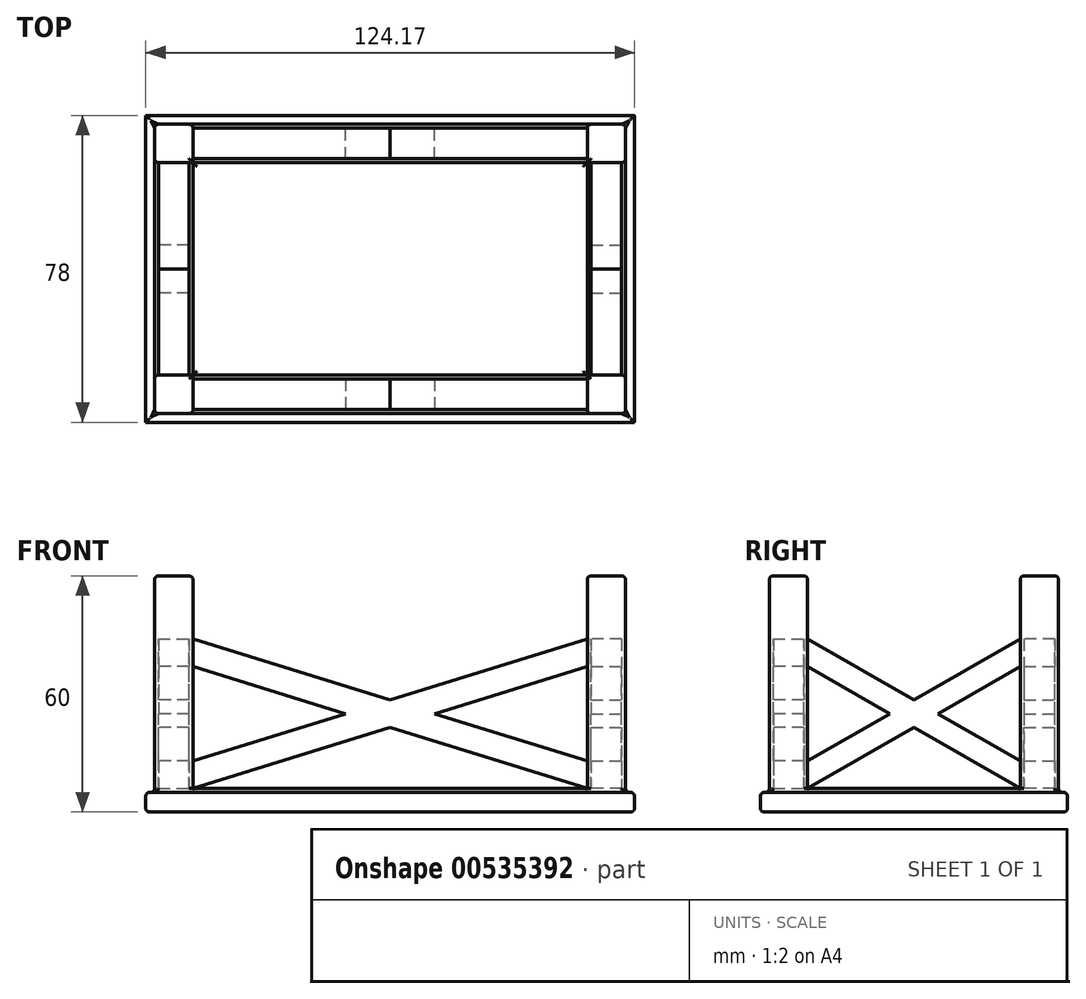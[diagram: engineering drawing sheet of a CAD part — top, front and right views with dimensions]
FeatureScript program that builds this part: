
annotation { "Feature Type Name" : "Feature", "Feature Type Description" : "" }
export const myFeature = defineFeature(function(context is Context, id is Id, definition is map)
    precondition{}
    {
        {
            var Q0;
            Q0=qCreatedBy(makeId("Top.planeOp"),FACE);
            var sketch = newSketch(context, id + "F0", { "sketchPlane" : qUnion([Q0])});
            skLineSegment(sketch, "E0.bottom", {"start": v(-35.73, 48.82) * mm, "end": v(88.44, 48.82) * mm});
            skLineSegment(sketch, "E0.top", {"start": v(-35.73, -29.18) * mm, "end": v(88.44, -29.18) * mm});
            skLineSegment(sketch, "E0.left", {"start": v(-35.73, 48.82) * mm, "end": v(-35.73, -29.18) * mm});
            skLineSegment(sketch, "E0.right", {"start": v(88.44, 48.82) * mm, "end": v(88.44, -29.18) * mm});
            skPoint(sketch, "E1", {"position": v(26.36, -29.18) * mm});
            skSolve(sketch);
        }
        {
            var Q0;
            Q0=qSketchRegion(id+"F0",true);
            extrude(context, id + "F1", {"entities" : qUnion([Q0]), "depth" : 5 * mm});
        }
        {
            var Q0;
            Q0=makeQuery(id+"F1.opExtrude","CAP_FACE",FACE,{"disambiguationData":[OSD([sQuery(id+"F0.wireOp",EDGE,"E0.bottom"),sQuery(id+"F0.wireOp",EDGE,"E0.top"),sQuery(id+"F0.wireOp",EDGE,"E0.left"),sQuery(id+"F0.wireOp",EDGE,"E0.right")])],"isStart":false});
            var sketch = newSketch(context, id + "F2", { "sketchPlane" : qUnion([Q0])});
            skLineSegment(sketch, "E2.bottom", {"start": v(-35.73, -29.18) * mm, "end": v(-23.73, -29.18) * mm, "construction": true});
            skLineSegment(sketch, "E2.top", {"start": v(-35.73, -17.18) * mm, "end": v(-23.73, -17.18) * mm, "construction": true});
            skLineSegment(sketch, "E2.left", {"start": v(-35.73, -29.18) * mm, "end": v(-35.73, -17.18) * mm, "construction": true});
            skLineSegment(sketch, "E2.right", {"start": v(-23.73, -29.18) * mm, "end": v(-23.73, -17.18) * mm, "construction": true});
            skLineSegment(sketch, "E3.bottom", {"start": v(88.44, 48.82) * mm, "end": v(76.44, 48.82) * mm, "construction": true});
            skLineSegment(sketch, "E3.top", {"start": v(88.44, 36.82) * mm, "end": v(76.44, 36.82) * mm, "construction": true});
            skLineSegment(sketch, "E3.left", {"start": v(88.44, 48.82) * mm, "end": v(88.44, 36.82) * mm, "construction": true});
            skLineSegment(sketch, "E3.right", {"start": v(76.44, 48.82) * mm, "end": v(76.44, 36.82) * mm, "construction": true});
            skLineSegment(sketch, "E4.bottom", {"start": v(88.44, -29.18) * mm, "end": v(76.44, -29.18) * mm, "construction": true});
            skLineSegment(sketch, "E4.top", {"start": v(88.44, -17.18) * mm, "end": v(76.44, -17.18) * mm, "construction": true});
            skLineSegment(sketch, "E4.left", {"start": v(88.44, -29.18) * mm, "end": v(88.44, -17.18) * mm, "construction": true});
            skLineSegment(sketch, "E4.right", {"start": v(76.44, -29.18) * mm, "end": v(76.44, -17.18) * mm, "construction": true});
            skLineSegment(sketch, "E5.bottom", {"start": v(-35.73, 48.82) * mm, "end": v(-23.73, 48.82) * mm, "construction": true});
            skLineSegment(sketch, "E5.top", {"start": v(-35.73, 36.82) * mm, "end": v(-23.73, 36.82) * mm, "construction": true});
            skLineSegment(sketch, "E5.left", {"start": v(-35.73, 48.82) * mm, "end": v(-35.73, 36.82) * mm, "construction": true});
            skLineSegment(sketch, "E5.right", {"start": v(-23.73, 48.82) * mm, "end": v(-23.73, 36.82) * mm, "construction": true});
            skLineSegment(sketch, "E6.bottom", {"start": v(-23.73, 36.82) * mm, "end": v(-33.48, 36.82) * mm});
            skLineSegment(sketch, "E6.top", {"start": v(-23.73, 46.57) * mm, "end": v(-33.48, 46.57) * mm});
            skLineSegment(sketch, "E6.left", {"start": v(-23.73, 36.82) * mm, "end": v(-23.73, 46.57) * mm});
            skLineSegment(sketch, "E6.right", {"start": v(-33.48, 36.82) * mm, "end": v(-33.48, 46.57) * mm});
            skLineSegment(sketch, "E7.bottom", {"start": v(-23.73, -17.18) * mm, "end": v(-33.48, -17.18) * mm});
            skLineSegment(sketch, "E7.top", {"start": v(-23.73, -26.93) * mm, "end": v(-33.48, -26.93) * mm});
            skLineSegment(sketch, "E7.left", {"start": v(-23.73, -17.18) * mm, "end": v(-23.73, -26.93) * mm});
            skLineSegment(sketch, "E7.right", {"start": v(-33.48, -17.18) * mm, "end": v(-33.48, -26.93) * mm});
            skLineSegment(sketch, "E8.bottom", {"start": v(76.44, 36.82) * mm, "end": v(86.2, 36.82) * mm});
            skLineSegment(sketch, "E8.top", {"start": v(76.44, 46.57) * mm, "end": v(86.2, 46.57) * mm});
            skLineSegment(sketch, "E8.left", {"start": v(76.44, 36.82) * mm, "end": v(76.44, 46.57) * mm});
            skLineSegment(sketch, "E8.right", {"start": v(86.2, 36.82) * mm, "end": v(86.2, 46.57) * mm});
            skLineSegment(sketch, "E9.bottom", {"start": v(76.44, -17.18) * mm, "end": v(86.2, -17.18) * mm});
            skLineSegment(sketch, "E9.top", {"start": v(76.44, -26.93) * mm, "end": v(86.2, -26.93) * mm});
            skLineSegment(sketch, "E9.left", {"start": v(76.44, -17.18) * mm, "end": v(76.44, -26.93) * mm});
            skLineSegment(sketch, "E9.right", {"start": v(86.2, -17.18) * mm, "end": v(86.2, -26.93) * mm});
            skSolve(sketch);
        }
        {
            var Q0;
            Q0=qSketchRegion(id+"F2",true);
            extrude(context, id + "F3", {"entities" : qUnion([Q0]), "operationType" : NewBodyOperationType.ADD, "depth" : 55 * mm});
        }
        {
            var Q0;
            Q0=makeQuery(id+"F3.opExtrude","SWEPT_FACE",FACE,{"disambiguationData":[OSD([sQuery(id+"F2.wireOp",EDGE,"E7.left")])]});
            var sketch = newSketch(context, id + "F4", { "sketchPlane" : qUnion([Q0])});
            skLineSegment(sketch, "E10.bottom", {"start": v(-25.93, 59) * mm, "end": v(-18.18, 59) * mm, "construction": true});
            skLineSegment(sketch, "E10.top", {"start": v(-25.93, 44) * mm, "end": v(-18.18, 44) * mm, "construction": true});
            skLineSegment(sketch, "E10.left", {"start": v(-25.93, 59) * mm, "end": v(-25.93, 44) * mm, "construction": true});
            skLineSegment(sketch, "E10.right", {"start": v(-18.18, 59) * mm, "end": v(-18.18, 44) * mm, "construction": true});
            skLineSegment(sketch, "E11.bottom", {"start": v(-25.93, 44) * mm, "end": v(-18.18, 44) * mm});
            skLineSegment(sketch, "E11.top", {"start": v(-25.93, 6) * mm, "end": v(-18.18, 6) * mm});
            skLineSegment(sketch, "E11.left", {"start": v(-25.93, 44) * mm, "end": v(-25.93, 6) * mm});
            skLineSegment(sketch, "E11.right", {"start": v(-18.18, 44) * mm, "end": v(-18.18, 6) * mm});
            skSolve(sketch);
        }
        {
            var Q0;
            Q0=qSketchRegion(id+"F4",true);
            extrude(context, id + "F5", {"entities" : qUnion([Q0]), "operationType" : NewBodyOperationType.ADD, "endBound" : BoundingType.UP_TO_NEXT, "depth" : 100.17 * mm});
        }
        {
            var Q0;
            Q0=makeQuery(id+"F5.opExtrude","SWEPT_FACE",FACE,{"disambiguationData":[OSD([sQuery(id+"F4.wireOp",EDGE,"E11.left")])]});
            var sketch = newSketch(context, id + "F6", { "sketchPlane" : qUnion([Q0])});
            skPoint(sketch, "E12", {"position": v(-23.73, 44) * mm});
            skPoint(sketch, "E13", {"position": v(-23.73, 37) * mm});
            skPoint(sketch, "E14", {"position": v(-23.73, 6) * mm});
            skPoint(sketch, "E15", {"position": v(-23.73, 13) * mm});
            skPoint(sketch, "E16", {"position": v(76.44, 44) * mm});
            skPoint(sketch, "E17", {"position": v(76.44, 37) * mm});
            skPoint(sketch, "E18", {"position": v(76.44, 6) * mm});
            skPoint(sketch, "E19", {"position": v(76.44, 13) * mm});
            skPoint(sketch, "E20", {"position": v(26.36, 28.5) * mm});
            skPoint(sketch, "E21", {"position": v(26.36, 21.5) * mm});
            skPoint(sketch, "E22", {"position": v(15.05, 25) * mm});
            skPoint(sketch, "E23", {"position": v(37.67, 25) * mm});
            skLineSegment(sketch, "E24", {"start": v(-23.73, 44) * mm, "end": v(76.44, 44) * mm});
            skLineSegment(sketch, "E25", {"start": v(26.36, 28.5) * mm, "end": v(76.44, 44) * mm});
            skLineSegment(sketch, "E26", {"start": v(-23.73, 44) * mm, "end": v(26.36, 28.5) * mm});
            skLineSegment(sketch, "E27", {"start": v(76.44, 37) * mm, "end": v(76.44, 13) * mm});
            skLineSegment(sketch, "E28", {"start": v(76.44, 13.06) * mm, "end": v(37.67, 25) * mm});
            skLineSegment(sketch, "E29", {"start": v(15.05, 25) * mm, "end": v(-23.73, 37) * mm});
            skLineSegment(sketch, "E30", {"start": v(15.05, 25) * mm, "end": v(-23.73, 13) * mm});
            skLineSegment(sketch, "E31", {"start": v(-23.73, 13) * mm, "end": v(-23.73, 37) * mm});
            skLineSegment(sketch, "E32", {"start": v(-23.73, 6) * mm, "end": v(76.44, 6) * mm});
            skLineSegment(sketch, "E33", {"start": v(26.36, 21.5) * mm, "end": v(76.44, 6) * mm});
            skLineSegment(sketch, "E34", {"start": v(26.36, 21.5) * mm, "end": v(-23.73, 6) * mm});
            skLineSegment(sketch, "E35", {"start": v(37.67, 25) * mm, "end": v(76.44, 37) * mm});
            skLineSegment(sketch, "E36", {"start": v(76.44, 37) * mm, "end": v(76.44, 13.06) * mm});
            skSolve(sketch);
        }
        {
            var Q0;
            Q0=qSketchRegion(id+"F6",true);
            extrude(context, id + "F7", {"entities" : qUnion([Q0]), "operationType" : NewBodyOperationType.REMOVE, "endBound" : BoundingType.UP_TO_NEXT, "oppositeDirection" : true, "depth" : 25 * mm});
        }
        {
            var Q0;
            Q0=makeQuery(id+"F3.opExtrude","SWEPT_FACE",FACE,{"disambiguationData":[OSD([sQuery(id+"F2.wireOp",EDGE,"E8.left")])]});
            var sketch = newSketch(context, id + "F8", { "sketchPlane" : qUnion([Q0])});
            skLineSegment(sketch, "E37.bottom", {"start": v(-45.57, 59) * mm, "end": v(-37.82, 59) * mm, "construction": true});
            skLineSegment(sketch, "E37.top", {"start": v(-45.57, 44) * mm, "end": v(-37.82, 44) * mm, "construction": true});
            skLineSegment(sketch, "E37.left", {"start": v(-45.57, 59) * mm, "end": v(-45.57, 44) * mm, "construction": true});
            skLineSegment(sketch, "E37.right", {"start": v(-37.82, 59) * mm, "end": v(-37.82, 44) * mm, "construction": true});
            skLineSegment(sketch, "E38.bottom", {"start": v(-45.57, 44) * mm, "end": v(-37.82, 44) * mm});
            skLineSegment(sketch, "E38.top", {"start": v(-45.57, 6) * mm, "end": v(-37.82, 6) * mm});
            skLineSegment(sketch, "E38.left", {"start": v(-45.57, 44) * mm, "end": v(-45.57, 6) * mm});
            skLineSegment(sketch, "E38.right", {"start": v(-37.82, 44) * mm, "end": v(-37.82, 6) * mm});
            skSolve(sketch);
        }
        {
            var Q0;
            Q0=qSketchRegion(id+"F8",true);
            extrude(context, id + "F9", {"entities" : qUnion([Q0]), "operationType" : NewBodyOperationType.ADD, "endBound" : BoundingType.UP_TO_NEXT, "depth" : 25 * mm});
        }
        {
            var Q0;
            Q0=makeQuery(id+"F9.opExtrude","SWEPT_FACE",FACE,{"disambiguationData":[OSD([sQuery(id+"F8.wireOp",EDGE,"E38.left")])]});
            var sketch = newSketch(context, id + "F10", { "sketchPlane" : qUnion([Q0])});
            skPoint(sketch, "E39", {"position": v(-76.44, 44) * mm});
            skPoint(sketch, "E40", {"position": v(-76.44, 37) * mm});
            skPoint(sketch, "E41", {"position": v(-76.44, 13) * mm});
            skPoint(sketch, "E42", {"position": v(-76.44, 6) * mm});
            skPoint(sketch, "E43", {"position": v(23.73, 44) * mm});
            skPoint(sketch, "E44", {"position": v(23.73, 37) * mm});
            skPoint(sketch, "E45", {"position": v(23.73, 13) * mm});
            skPoint(sketch, "E46", {"position": v(23.73, 6) * mm});
            skLineSegment(sketch, "E47", {"start": v(-76.44, 37) * mm, "end": v(23.73, 6) * mm, "construction": true});
            skLineSegment(sketch, "E48", {"start": v(-76.44, 44) * mm, "end": v(23.73, 13) * mm, "construction": true});
            skLineSegment(sketch, "E49", {"start": v(23.73, 44) * mm, "end": v(-76.44, 13) * mm, "construction": true});
            skLineSegment(sketch, "E50", {"start": v(-76.44, 6) * mm, "end": v(23.73, 37) * mm, "construction": true});
            skLineSegment(sketch, "E51", {"start": v(-76.44, 44) * mm, "end": v(-26.36, 28.5) * mm});
            skLineSegment(sketch, "E52", {"start": v(-26.36, 28.5) * mm, "end": v(23.73, 44) * mm});
            skLineSegment(sketch, "E53", {"start": v(-76.44, 44) * mm, "end": v(23.73, 44) * mm});
            skLineSegment(sketch, "E54", {"start": v(-76.44, 13) * mm, "end": v(-76.44, 37) * mm});
            skLineSegment(sketch, "E55", {"start": v(-76.44, 37) * mm, "end": v(-37.67, 25) * mm});
            skLineSegment(sketch, "E56", {"start": v(-37.67, 25) * mm, "end": v(-76.44, 13) * mm});
            skLineSegment(sketch, "E57", {"start": v(-76.44, 6) * mm, "end": v(23.73, 6) * mm});
            skLineSegment(sketch, "E58", {"start": v(-26.36, 21.5) * mm, "end": v(23.73, 6) * mm});
            skLineSegment(sketch, "E59", {"start": v(-76.44, 6) * mm, "end": v(-26.36, 21.5) * mm});
            skLineSegment(sketch, "E60", {"start": v(23.73, 37) * mm, "end": v(23.73, 13) * mm});
            skLineSegment(sketch, "E61", {"start": v(23.73, 13) * mm, "end": v(-15.05, 25) * mm});
            skLineSegment(sketch, "E62", {"start": v(-15.05, 25) * mm, "end": v(23.73, 37) * mm});
            skSolve(sketch);
        }
        {
            var Q0;
            Q0=qSketchRegion(id+"F10",true);
            extrude(context, id + "F11", {"entities" : qUnion([Q0]), "operationType" : NewBodyOperationType.REMOVE, "endBound" : BoundingType.UP_TO_NEXT, "oppositeDirection" : true, "depth" : 25 * mm});
        }
        {
            var Q0;
            Q0=makeQuery(id+"F3.opExtrude","SWEPT_FACE",FACE,{"disambiguationData":[OSD([sQuery(id+"F2.wireOp",EDGE,"E6.bottom")])]});
            var sketch = newSketch(context, id + "F12", { "sketchPlane" : qUnion([Q0])});
            skLineSegment(sketch, "E63.bottom", {"start": v(-32.48, 59) * mm, "end": v(-24.73, 59) * mm, "construction": true});
            skLineSegment(sketch, "E63.top", {"start": v(-32.48, 44) * mm, "end": v(-24.73, 44) * mm, "construction": true});
            skLineSegment(sketch, "E63.left", {"start": v(-32.48, 59) * mm, "end": v(-32.48, 44) * mm, "construction": true});
            skLineSegment(sketch, "E63.right", {"start": v(-24.73, 59) * mm, "end": v(-24.73, 44) * mm, "construction": true});
            skLineSegment(sketch, "E64.bottom", {"start": v(-32.48, 44) * mm, "end": v(-24.73, 44) * mm});
            skLineSegment(sketch, "E64.top", {"start": v(-32.48, 6) * mm, "end": v(-24.73, 6) * mm});
            skLineSegment(sketch, "E64.left", {"start": v(-32.48, 44) * mm, "end": v(-32.48, 6) * mm});
            skLineSegment(sketch, "E64.right", {"start": v(-24.73, 44) * mm, "end": v(-24.73, 6) * mm});
            skSolve(sketch);
        }
        {
            var Q0;
            Q0=qSketchRegion(id+"F12",true);
            extrude(context, id + "F13", {"entities" : qUnion([Q0]), "operationType" : NewBodyOperationType.ADD, "endBound" : BoundingType.UP_TO_NEXT, "depth" : 25 * mm});
        }
        {
            var Q0;
            Q0=makeQuery(id+"F13.opExtrude","SWEPT_FACE",FACE,{"disambiguationData":[OSD([sQuery(id+"F12.wireOp",EDGE,"E64.left")])]});
            var sketch = newSketch(context, id + "F14", { "sketchPlane" : qUnion([Q0])});
            skPoint(sketch, "E65", {"position": v(-36.82, 44) * mm});
            skPoint(sketch, "E66", {"position": v(-36.82, 37) * mm});
            skPoint(sketch, "E67", {"position": v(-36.82, 13) * mm});
            skPoint(sketch, "E68", {"position": v(-36.82, 6) * mm});
            skPoint(sketch, "E69", {"position": v(17.18, 6) * mm});
            skPoint(sketch, "E70", {"position": v(17.18, 13) * mm});
            skPoint(sketch, "E71", {"position": v(17.18, 37) * mm});
            skPoint(sketch, "E72", {"position": v(17.18, 44) * mm});
            skLineSegment(sketch, "E73", {"start": v(-36.82, 37) * mm, "end": v(17.18, 6) * mm, "construction": true});
            skLineSegment(sketch, "E74", {"start": v(17.18, 13) * mm, "end": v(-36.82, 44) * mm, "construction": true});
            skLineSegment(sketch, "E75", {"start": v(-36.82, 13) * mm, "end": v(17.18, 44) * mm, "construction": true});
            skLineSegment(sketch, "E76", {"start": v(17.18, 37) * mm, "end": v(-36.82, 6) * mm, "construction": true});
            skLineSegment(sketch, "E77", {"start": v(-36.82, 44) * mm, "end": v(17.18, 44) * mm});
            skLineSegment(sketch, "E78", {"start": v(-9.82, 28.5) * mm, "end": v(17.18, 44) * mm});
            skLineSegment(sketch, "E79", {"start": v(-9.82, 28.5) * mm, "end": v(-36.82, 44) * mm});
            skLineSegment(sketch, "E80", {"start": v(-36.82, 37) * mm, "end": v(-36.82, 13) * mm});
            skLineSegment(sketch, "E81", {"start": v(-36.82, 13) * mm, "end": v(-15.92, 25) * mm});
            skLineSegment(sketch, "E82", {"start": v(-15.92, 25) * mm, "end": v(-36.82, 37) * mm});
            skLineSegment(sketch, "E83", {"start": v(17.18, 37) * mm, "end": v(17.18, 13) * mm});
            skLineSegment(sketch, "E84", {"start": v(17.18, 13) * mm, "end": v(-3.72, 25) * mm});
            skLineSegment(sketch, "E85", {"start": v(17.18, 37) * mm, "end": v(-3.72, 25) * mm});
            skLineSegment(sketch, "E86", {"start": v(-36.82, 6) * mm, "end": v(17.18, 6) * mm});
            skLineSegment(sketch, "E87", {"start": v(17.18, 6) * mm, "end": v(-9.82, 21.5) * mm});
            skLineSegment(sketch, "E88", {"start": v(-36.82, 6) * mm, "end": v(-9.82, 21.5) * mm});
            skSolve(sketch);
        }
        {
            var Q0;
            Q0=qSketchRegion(id+"F14",true);
            extrude(context, id + "F15", {"entities" : qUnion([Q0]), "operationType" : NewBodyOperationType.REMOVE, "endBound" : BoundingType.UP_TO_NEXT, "oppositeDirection" : true, "depth" : 25 * mm});
        }
        {
            var Q0;
            Q0=makeQuery(id+"F3.opExtrude","SWEPT_FACE",FACE,{"disambiguationData":[OSD([sQuery(id+"F2.wireOp",EDGE,"E9.bottom")])]});
            var sketch = newSketch(context, id + "F16", { "sketchPlane" : qUnion([Q0])});
            skLineSegment(sketch, "E89.bottom", {"start": v(-85.2, 59) * mm, "end": v(-77.44, 59) * mm, "construction": true});
            skLineSegment(sketch, "E89.top", {"start": v(-85.2, 44) * mm, "end": v(-77.44, 44) * mm, "construction": true});
            skLineSegment(sketch, "E89.left", {"start": v(-85.2, 59) * mm, "end": v(-85.2, 44) * mm, "construction": true});
            skLineSegment(sketch, "E89.right", {"start": v(-77.44, 59) * mm, "end": v(-77.44, 44) * mm, "construction": true});
            skLineSegment(sketch, "E90.bottom", {"start": v(-85.2, 44) * mm, "end": v(-77.44, 44) * mm});
            skLineSegment(sketch, "E90.top", {"start": v(-85.2, 6) * mm, "end": v(-77.44, 6) * mm});
            skLineSegment(sketch, "E90.left", {"start": v(-85.2, 44) * mm, "end": v(-85.2, 6) * mm});
            skLineSegment(sketch, "E90.right", {"start": v(-77.44, 44) * mm, "end": v(-77.44, 6) * mm});
            skSolve(sketch);
        }
        {
            var Q0;
            Q0=qSketchRegion(id+"F16",true);
            extrude(context, id + "F17", {"entities" : qUnion([Q0]), "operationType" : NewBodyOperationType.ADD, "endBound" : BoundingType.UP_TO_NEXT, "depth" : 25 * mm});
        }
        {
            var Q0;
            Q0=makeQuery(id+"F17.opExtrude","SWEPT_FACE",FACE,{"disambiguationData":[OSD([sQuery(id+"F16.wireOp",EDGE,"E90.left")])]});
            var sketch = newSketch(context, id + "F18", { "sketchPlane" : qUnion([Q0])});
            skPoint(sketch, "E91", {"position": v(-17.18, 44) * mm});
            skPoint(sketch, "E92", {"position": v(-17.18, 37) * mm});
            skPoint(sketch, "E93", {"position": v(-17.18, 13) * mm});
            skPoint(sketch, "E94", {"position": v(-17.18, 6) * mm});
            skPoint(sketch, "E95", {"position": v(36.82, 44) * mm});
            skPoint(sketch, "E96", {"position": v(36.82, 37) * mm});
            skPoint(sketch, "E97", {"position": v(36.82, 13) * mm});
            skPoint(sketch, "E98", {"position": v(36.82, 6) * mm});
            skLineSegment(sketch, "E99", {"start": v(-17.18, 44) * mm, "end": v(36.82, 13) * mm, "construction": true});
            skLineSegment(sketch, "E100", {"start": v(36.82, 6) * mm, "end": v(-17.18, 37) * mm, "construction": true});
            skLineSegment(sketch, "E101", {"start": v(36.82, 44) * mm, "end": v(-17.18, 13) * mm, "construction": true});
            skLineSegment(sketch, "E102", {"start": v(-17.18, 6) * mm, "end": v(36.82, 37) * mm, "construction": true});
            skLineSegment(sketch, "E103", {"start": v(-17.18, 44) * mm, "end": v(36.82, 44) * mm});
            skLineSegment(sketch, "E104", {"start": v(36.82, 44) * mm, "end": v(9.82, 28.5) * mm});
            skLineSegment(sketch, "E105", {"start": v(9.82, 28.5) * mm, "end": v(-17.18, 44) * mm});
            skLineSegment(sketch, "E106", {"start": v(-17.18, 37) * mm, "end": v(-17.18, 13) * mm});
            skLineSegment(sketch, "E107", {"start": v(-17.18, 13) * mm, "end": v(3.72, 25) * mm});
            skLineSegment(sketch, "E108", {"start": v(-17.18, 37) * mm, "end": v(3.72, 25) * mm});
            skLineSegment(sketch, "E109", {"start": v(36.82, 37) * mm, "end": v(36.82, 13) * mm});
            skLineSegment(sketch, "E110", {"start": v(36.82, 13) * mm, "end": v(15.92, 25) * mm});
            skLineSegment(sketch, "E111", {"start": v(15.92, 25) * mm, "end": v(36.82, 37) * mm});
            skLineSegment(sketch, "E112", {"start": v(-17.18, 6) * mm, "end": v(36.82, 6) * mm});
            skLineSegment(sketch, "E113", {"start": v(36.82, 6) * mm, "end": v(9.82, 21.5) * mm});
            skLineSegment(sketch, "E114", {"start": v(9.82, 21.5) * mm, "end": v(-17.18, 6) * mm});
            skSolve(sketch);
        }
        {
            var Q0;
            Q0=qSketchRegion(id+"F18",true);
            extrude(context, id + "F19", {"entities" : qUnion([Q0]), "operationType" : NewBodyOperationType.REMOVE, "endBound" : BoundingType.UP_TO_NEXT, "oppositeDirection" : true, "depth" : 25 * mm});
        }
        {
            var Q0;
            Q0=makeQuery(id+"F15.boolean.opBoolean","MERGE",FACE,{"derivedFrom":[makeQuery(id+"F3.opExtrude","SWEPT_FACE",FACE,{"disambiguationData":[OSD([sQuery(id+"F2.wireOp",EDGE,"E7.bottom")])]}),makeQuery(id+"F15.opExtrude","SWEPT_FACE",FACE,{"disambiguationData":[OSD([sQuery(id+"F14.wireOp",EDGE,"E83")])]})]});
            var sketch = newSketch(context, id + "F20", { "sketchPlane" : qUnion([Q0])});
            skLineSegment(sketch, "E115.bottom", {"start": v(33.48, 5) * mm, "end": v(23.73, 5) * mm});
            skLineSegment(sketch, "E115.top", {"start": v(33.48, 6) * mm, "end": v(23.73, 6) * mm});
            skLineSegment(sketch, "E115.left", {"start": v(33.48, 5) * mm, "end": v(33.48, 6) * mm});
            skLineSegment(sketch, "E115.right", {"start": v(23.73, 5) * mm, "end": v(23.73, 6) * mm});
            skSolve(sketch);
        }
        {
            var Q0;
            Q0=qSketchRegion(id+"F20",true);
            extrude(context, id + "F21", {"entities" : qUnion([Q0]), "operationType" : NewBodyOperationType.ADD, "endBound" : BoundingType.UP_TO_NEXT, "depth" : 25 * mm});
        }
        {
            var Q0;
            Q0=makeQuery(id+"F21.boolean.opBoolean","MERGE",FACE,{"derivedFrom":[makeQuery(id+"F7.boolean.opBoolean","MERGE",FACE,{"derivedFrom":[makeQuery(id+"F3.opExtrude","SWEPT_FACE",FACE,{"disambiguationData":[OSD([sQuery(id+"F2.wireOp",EDGE,"E7.left")])]}),makeQuery(id+"F7.opExtrude","SWEPT_FACE",FACE,{"disambiguationData":[OSD([sQuery(id+"F6.wireOp",EDGE,"E31")])]})]}),makeQuery(id+"F11.boolean.opBoolean","MERGE",FACE,{"derivedFrom":[makeQuery(id+"F3.opExtrude","SWEPT_FACE",FACE,{"disambiguationData":[OSD([sQuery(id+"F2.wireOp",EDGE,"E6.left")])]}),makeQuery(id+"F11.opExtrude","SWEPT_FACE",FACE,{"disambiguationData":[OSD([sQuery(id+"F10.wireOp",EDGE,"E60")])]})]}),makeQuery(id+"F21.opExtrude","SWEPT_FACE",FACE,{"disambiguationData":[OSD([sQuery(id+"F20.wireOp",EDGE,"E115.right")])]})]});
            var sketch = newSketch(context, id + "F22", { "sketchPlane" : qUnion([Q0])});
            skLineSegment(sketch, "E116.bottom", {"start": v(46.57, 5) * mm, "end": v(36.82, 5) * mm});
            skLineSegment(sketch, "E116.top", {"start": v(46.57, 6) * mm, "end": v(36.82, 6) * mm});
            skLineSegment(sketch, "E116.left", {"start": v(46.57, 5) * mm, "end": v(46.57, 6) * mm});
            skLineSegment(sketch, "E116.right", {"start": v(36.82, 5) * mm, "end": v(36.82, 6) * mm});
            skSolve(sketch);
        }
        {
            var Q0;
            Q0=qSketchRegion(id+"F22",true);
            extrude(context, id + "F23", {"entities" : qUnion([Q0]), "operationType" : NewBodyOperationType.ADD, "endBound" : BoundingType.UP_TO_NEXT, "depth" : 25 * mm});
        }
        {
            var Q0;
            Q0=makeQuery(id+"F23.boolean.opBoolean","MERGE",FACE,{"derivedFrom":[makeQuery(id+"F19.boolean.opBoolean","MERGE",FACE,{"derivedFrom":[makeQuery(id+"F3.opExtrude","SWEPT_FACE",FACE,{"disambiguationData":[OSD([sQuery(id+"F2.wireOp",EDGE,"E8.bottom")])]}),makeQuery(id+"F19.opExtrude","SWEPT_FACE",FACE,{"disambiguationData":[OSD([sQuery(id+"F18.wireOp",EDGE,"E109")])]})]}),makeQuery(id+"F23.opExtrude","SWEPT_FACE",FACE,{"disambiguationData":[OSD([sQuery(id+"F22.wireOp",EDGE,"E116.right")])]})]});
            var sketch = newSketch(context, id + "F24", { "sketchPlane" : qUnion([Q0])});
            skLineSegment(sketch, "E117.bottom", {"start": v(86.2, 5) * mm, "end": v(76.44, 5) * mm});
            skLineSegment(sketch, "E117.top", {"start": v(86.2, 6) * mm, "end": v(76.44, 6) * mm});
            skLineSegment(sketch, "E117.left", {"start": v(86.2, 5) * mm, "end": v(86.2, 6) * mm});
            skLineSegment(sketch, "E117.right", {"start": v(76.44, 5) * mm, "end": v(76.44, 6) * mm});
            skSolve(sketch);
        }
        {
            var Q0;
            Q0=qSketchRegion(id+"F24",true);
            extrude(context, id + "F25", {"entities" : qUnion([Q0]), "operationType" : NewBodyOperationType.ADD, "endBound" : BoundingType.UP_TO_NEXT, "depth" : 25 * mm});
        }
        {
            var Q0;
            Q0=makeQuery(id+"F25.boolean.opBoolean","MERGE",FACE,{"derivedFrom":[makeQuery(id+"F3.opExtrude","SWEPT_FACE",FACE,{"disambiguationData":[OSD([sQuery(id+"F2.wireOp",EDGE,"E9.left")])]}),makeQuery(id+"F25.opExtrude","SWEPT_FACE",FACE,{"disambiguationData":[OSD([sQuery(id+"F24.wireOp",EDGE,"E117.right")])]})]});
            var sketch = newSketch(context, id + "F26", { "sketchPlane" : qUnion([Q0])});
            skLineSegment(sketch, "E118.bottom", {"start": v(26.93, 5) * mm, "end": v(17.18, 5) * mm});
            skLineSegment(sketch, "E118.top", {"start": v(26.93, 6) * mm, "end": v(17.18, 6) * mm});
            skLineSegment(sketch, "E118.left", {"start": v(26.93, 5) * mm, "end": v(26.93, 6) * mm});
            skLineSegment(sketch, "E118.right", {"start": v(17.18, 5) * mm, "end": v(17.18, 6) * mm});
            skSolve(sketch);
        }
        {
            var Q0;
            Q0=qSketchRegion(id+"F26",true);
            extrude(context, id + "F27", {"entities" : qUnion([Q0]), "operationType" : NewBodyOperationType.ADD, "endBound" : BoundingType.UP_TO_NEXT, "depth" : 25 * mm});
        }
        {
            var Q0;
            Q0=makeQuery(id+"F1.opExtrude","CAP_FACE",FACE,{"disambiguationData":[OSD([sQuery(id+"F0.wireOp",EDGE,"E0.bottom"),sQuery(id+"F0.wireOp",EDGE,"E0.top"),sQuery(id+"F0.wireOp",EDGE,"E0.left"),sQuery(id+"F0.wireOp",EDGE,"E0.right")])],"isStart":true});
            var Q1;
            Q1=makeQuery(id+"F27.boolean.opBoolean","SPLIT",FACE,{"disambiguationData":[TD([makeQuery(id+"F3.opExtrude","SWEPT_FACE",FACE,{"disambiguationData":[OSD([sQuery(id+"F2.wireOp",EDGE,"E6.left")])]})])],"derivedFrom":makeQuery(id+"F1.opExtrude","CAP_FACE",FACE,{"disambiguationData":[OSD([sQuery(id+"F0.wireOp",EDGE,"E0.bottom"),sQuery(id+"F0.wireOp",EDGE,"E0.top"),sQuery(id+"F0.wireOp",EDGE,"E0.left"),sQuery(id+"F0.wireOp",EDGE,"E0.right")])],"isStart":false})});
            var Q2;
            {var subQ0=sQuery(id+"F0.wireOp",EDGE,"E0.bottom");var subQ1=sQuery(id+"F0.wireOp",EDGE,"E0.right");var subQ2=sQuery(id+"F0.wireOp",EDGE,"E0.top");var subQ3=sQuery(id+"F0.wireOp",EDGE,"E0.left");Q2=makeQuery(id+"F27.boolean.opBoolean","SPLIT",FACE,{"disambiguationData":[TD([makeQuery(id+"F1.opExtrude","SWEPT_FACE",FACE,{"disambiguationData":[OSD([subQ0])]})])],"derivedFrom":makeQuery(id+"F1.opExtrude","CAP_FACE",FACE,{"disambiguationData":[OSD([subQ0,subQ2,subQ3,subQ1])],"isStart":false})});}
            var Q3;
            Q3=makeQuery(id+"F3.opExtrude","CAP_FACE",FACE,{"disambiguationData":[OSD([sQuery(id+"F2.wireOp",EDGE,"E8.bottom"),sQuery(id+"F2.wireOp",EDGE,"E8.top"),sQuery(id+"F2.wireOp",EDGE,"E8.left"),sQuery(id+"F2.wireOp",EDGE,"E8.right")])],"isStart":false});
            var Q4;
            Q4=makeQuery(id+"F3.opExtrude","CAP_FACE",FACE,{"disambiguationData":[OSD([sQuery(id+"F2.wireOp",EDGE,"E7.bottom"),sQuery(id+"F2.wireOp",EDGE,"E7.top"),sQuery(id+"F2.wireOp",EDGE,"E7.left"),sQuery(id+"F2.wireOp",EDGE,"E7.right")])],"isStart":false});
            var Q5;
            Q5=makeQuery(id+"F3.opExtrude","CAP_FACE",FACE,{"disambiguationData":[OSD([sQuery(id+"F2.wireOp",EDGE,"E6.bottom"),sQuery(id+"F2.wireOp",EDGE,"E6.top"),sQuery(id+"F2.wireOp",EDGE,"E6.left"),sQuery(id+"F2.wireOp",EDGE,"E6.right")])],"isStart":false});
            var Q6;
            Q6=makeQuery(id+"F3.opExtrude","CAP_FACE",FACE,{"disambiguationData":[OSD([sQuery(id+"F2.wireOp",EDGE,"E9.bottom"),sQuery(id+"F2.wireOp",EDGE,"E9.top"),sQuery(id+"F2.wireOp",EDGE,"E9.left"),sQuery(id+"F2.wireOp",EDGE,"E9.right")])],"isStart":false});
            fillet(context, id + "F28", {"entities" : qUnion([Q0, Q1, Q2, Q3, Q4, Q5, Q6]), "radius" : 1 * mm, "tangentPropagation" : true, "allowEdgeOverflow" : false});
        }
        {
            var Q0;
            Q0=makeQuery(id+"F28.opFillet","SPLIT",FACE,{"disambiguationData":[OD(1.0)],"derivedFrom":makeQuery(id+"F25.boolean.opBoolean","MERGE",FACE,{"derivedFrom":[makeQuery(id+"F3.opExtrude","SWEPT_FACE",FACE,{"disambiguationData":[OSD([sQuery(id+"F2.wireOp",EDGE,"E8.right")])]}),makeQuery(id+"F3.opExtrude","SWEPT_FACE",FACE,{"disambiguationData":[OSD([sQuery(id+"F2.wireOp",EDGE,"E9.right")])]}),makeQuery(id+"F25.opExtrude","SWEPT_FACE",FACE,{"disambiguationData":[OSD([sQuery(id+"F24.wireOp",EDGE,"E117.left")])]})]})});
            var Q1;
            Q1=makeQuery(id+"F28.opFillet","SPLIT",FACE,{"disambiguationData":[OD(1.0)],"derivedFrom":makeQuery(id+"F27.boolean.opBoolean","MERGE",FACE,{"derivedFrom":[makeQuery(id+"F3.opExtrude","SWEPT_FACE",FACE,{"disambiguationData":[OSD([sQuery(id+"F2.wireOp",EDGE,"E7.top")])]}),makeQuery(id+"F3.opExtrude","SWEPT_FACE",FACE,{"disambiguationData":[OSD([sQuery(id+"F2.wireOp",EDGE,"E9.top")])]}),makeQuery(id+"F27.opExtrude","SWEPT_FACE",FACE,{"disambiguationData":[OSD([sQuery(id+"F26.wireOp",EDGE,"E118.left")])]})]})});
            var Q2;
            Q2=makeQuery(id+"F28.opFillet","SPLIT",FACE,{"disambiguationData":[OD(0.0)],"derivedFrom":makeQuery(id+"F27.boolean.opBoolean","MERGE",FACE,{"derivedFrom":[makeQuery(id+"F3.opExtrude","SWEPT_FACE",FACE,{"disambiguationData":[OSD([sQuery(id+"F2.wireOp",EDGE,"E7.top")])]}),makeQuery(id+"F3.opExtrude","SWEPT_FACE",FACE,{"disambiguationData":[OSD([sQuery(id+"F2.wireOp",EDGE,"E9.top")])]}),makeQuery(id+"F27.opExtrude","SWEPT_FACE",FACE,{"disambiguationData":[OSD([sQuery(id+"F26.wireOp",EDGE,"E118.left")])]})]})});
            var Q3;
            Q3=makeQuery(id+"F28.opFillet","SPLIT",FACE,{"disambiguationData":[OD(1.0)],"derivedFrom":makeQuery(id+"F21.boolean.opBoolean","MERGE",FACE,{"derivedFrom":[makeQuery(id+"F3.opExtrude","SWEPT_FACE",FACE,{"disambiguationData":[OSD([sQuery(id+"F2.wireOp",EDGE,"E6.right")])]}),makeQuery(id+"F3.opExtrude","SWEPT_FACE",FACE,{"disambiguationData":[OSD([sQuery(id+"F2.wireOp",EDGE,"E7.right")])]}),makeQuery(id+"F21.opExtrude","SWEPT_FACE",FACE,{"disambiguationData":[OSD([sQuery(id+"F20.wireOp",EDGE,"E115.left")])]})]})});
            var Q4;
            Q4=makeQuery(id+"F28.opFillet","SPLIT",FACE,{"disambiguationData":[OD(0.0)],"derivedFrom":makeQuery(id+"F21.boolean.opBoolean","MERGE",FACE,{"derivedFrom":[makeQuery(id+"F3.opExtrude","SWEPT_FACE",FACE,{"disambiguationData":[OSD([sQuery(id+"F2.wireOp",EDGE,"E6.right")])]}),makeQuery(id+"F3.opExtrude","SWEPT_FACE",FACE,{"disambiguationData":[OSD([sQuery(id+"F2.wireOp",EDGE,"E7.right")])]}),makeQuery(id+"F21.opExtrude","SWEPT_FACE",FACE,{"disambiguationData":[OSD([sQuery(id+"F20.wireOp",EDGE,"E115.left")])]})]})});
            var Q5;
            Q5=makeQuery(id+"F28.opFillet","SPLIT",FACE,{"disambiguationData":[OD(0.0)],"derivedFrom":makeQuery(id+"F23.boolean.opBoolean","MERGE",FACE,{"derivedFrom":[makeQuery(id+"F3.opExtrude","SWEPT_FACE",FACE,{"disambiguationData":[OSD([sQuery(id+"F2.wireOp",EDGE,"E6.top")])]}),makeQuery(id+"F3.opExtrude","SWEPT_FACE",FACE,{"disambiguationData":[OSD([sQuery(id+"F2.wireOp",EDGE,"E8.top")])]}),makeQuery(id+"F23.opExtrude","SWEPT_FACE",FACE,{"disambiguationData":[OSD([sQuery(id+"F22.wireOp",EDGE,"E116.left")])]})]})});
            var Q6;
            Q6=makeQuery(id+"F28.opFillet","SPLIT",FACE,{"disambiguationData":[OD(1.0)],"derivedFrom":makeQuery(id+"F23.boolean.opBoolean","MERGE",FACE,{"derivedFrom":[makeQuery(id+"F3.opExtrude","SWEPT_FACE",FACE,{"disambiguationData":[OSD([sQuery(id+"F2.wireOp",EDGE,"E6.top")])]}),makeQuery(id+"F3.opExtrude","SWEPT_FACE",FACE,{"disambiguationData":[OSD([sQuery(id+"F2.wireOp",EDGE,"E8.top")])]}),makeQuery(id+"F23.opExtrude","SWEPT_FACE",FACE,{"disambiguationData":[OSD([sQuery(id+"F22.wireOp",EDGE,"E116.left")])]})]})});
            var Q7;
            Q7=makeQuery(id+"F28.opFillet","SPLIT",FACE,{"disambiguationData":[OD(0.0)],"derivedFrom":makeQuery(id+"F25.boolean.opBoolean","MERGE",FACE,{"derivedFrom":[makeQuery(id+"F3.opExtrude","SWEPT_FACE",FACE,{"disambiguationData":[OSD([sQuery(id+"F2.wireOp",EDGE,"E8.right")])]}),makeQuery(id+"F3.opExtrude","SWEPT_FACE",FACE,{"disambiguationData":[OSD([sQuery(id+"F2.wireOp",EDGE,"E9.right")])]}),makeQuery(id+"F25.opExtrude","SWEPT_FACE",FACE,{"disambiguationData":[OSD([sQuery(id+"F24.wireOp",EDGE,"E117.left")])]})]})});
            fillet(context, id + "F29", {"entities" : qUnion([Q0, Q1, Q2, Q3, Q4, Q5, Q6, Q7]), "radius" : 1 * mm, "tangentPropagation" : true, "allowEdgeOverflow" : false});
        }
    });
